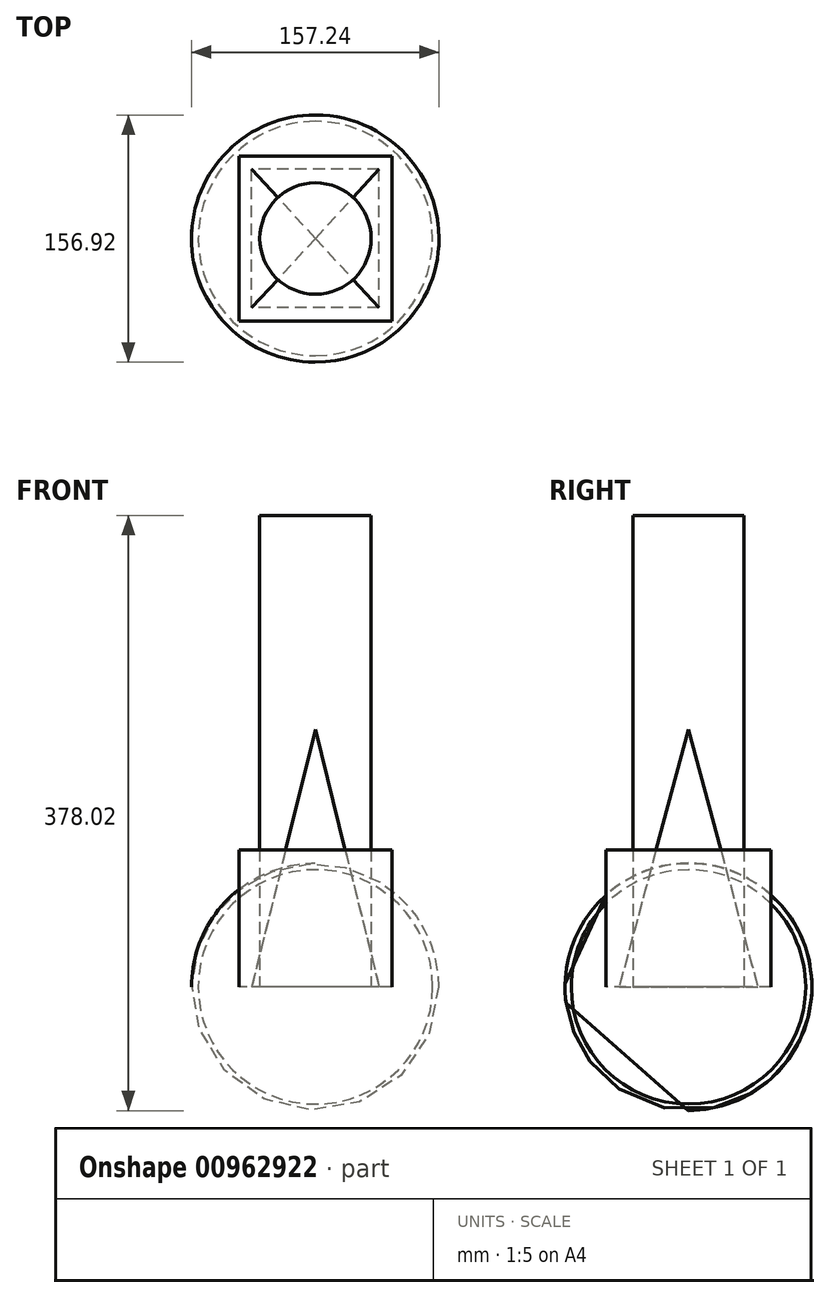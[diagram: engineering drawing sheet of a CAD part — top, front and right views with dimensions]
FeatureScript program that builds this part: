
annotation { "Feature Type Name" : "Feature", "Feature Type Description" : "" }
export const myFeature = defineFeature(function(context is Context, id is Id, definition is map)
    precondition{}
    {
        {
            var Q0;
            Q0=qCreatedBy(makeId("Top.planeOp"),FACE);
            var sketch = newSketch(context, id + "F0", { "sketchPlane" : qUnion([Q0])});
            skArc(sketch, "E0", {"start": v(0, 78.46) * mm, "mid": v(-78.46, 0.16) * mm, "end": v(-0.32, -78.46) * mm});
            skLineSegment(sketch, "E1", {"start": v(0, 78.46) * mm, "end": v(-0.32, -78.46) * mm});
            skSolve(sketch);
        }
        {
            var Q0;
            Q0=makeQuery(id+"F0.imprint","IMPRINT",FACE,{"disambiguationData":[TD([[makeQuery(id+"F0.imprint","IMPRINT",EDGE,{"derivedFrom":sQuery(id+"F0.wireOp",EDGE,"E0")}),1.0]])]});
            var Q1;
            Q1=sQuery(id+"F0.wireOp",EDGE,"E1");
            revolve(context, id + "F1", {"surfaceOperationType" : NewSurfaceOperationType.NEW, "entities" : qUnion([Q0]), "axis" : qUnion([Q1]), "revolveType" : RevolveType.FULL});
        }
        {
            var Q0;
            Q0=qCreatedBy(makeId("Top.planeOp"),FACE);
            var sketch = newSketch(context, id + "F2", { "sketchPlane" : qUnion([Q0])});
            skLineSegment(sketch, "E2.bottom", {"start": v(40.46, -44) * mm, "end": v(-40.46, -44) * mm});
            skLineSegment(sketch, "E2.top", {"start": v(40.46, 44) * mm, "end": v(-40.46, 44) * mm});
            skLineSegment(sketch, "E2.left", {"start": v(40.46, -44) * mm, "end": v(40.46, 44) * mm});
            skLineSegment(sketch, "E2.right", {"start": v(-40.46, -44) * mm, "end": v(-40.46, 44) * mm});
            skPoint(sketch, "E2.middle", {"position": v(0, 0) * mm});
            skSolve(sketch);
        }
        {
            var Q0;
            Q0=qCreatedBy(makeId("Front.planeOp"),FACE);
            var sketch = newSketch(context, id + "F3", { "sketchPlane" : qUnion([Q0])});
            skPoint(sketch, "E3", {"position": v(0, 163.51) * mm});
            skSolve(sketch);
        }
        {
            var Q0;
            Q0=sQuery(id+"F3.wireOp",VERTEX,"E3");
            var Q1;
            Q1 = qSketchRegion(id + "F2", true);
            loft(context, id + "F4", {"sheetProfilesArray" : [{ "sheetProfileEntities" : qUnion([Q0]) }, { "sheetProfileEntities" : qUnion([Q1]) }]});
        }
        {
            var Q0;
            Q0=qCreatedBy(makeId("Top.planeOp"),FACE);
            var sketch = newSketch(context, id + "F5", { "sketchPlane" : qUnion([Q0])});
            skCircle(sketch, "E4", {"center": v(0, 0) * mm, "radius": 35.35 * mm});
            skSolve(sketch);
        }
        {
            var Q0;
            Q0=makeQuery(id+"F5.imprint","IMPRINT",FACE,{"disambiguationData":[TD([[makeQuery(id+"F5.imprint","IMPRINT",EDGE,{"derivedFrom":sQuery(id+"F5.wireOp",EDGE,"E4")}),1.0]])]});
            extrude(context, id + "F6", {"entities" : qUnion([Q0]), "depth" : 299.4 * mm, "offsetDistance" : 25.4 * mm});
        }
        {
            var Q0;
            Q0=qCreatedBy(makeId("Top.planeOp"),FACE);
            var sketch = newSketch(context, id + "F7", { "sketchPlane" : qUnion([Q0])});
            skArc(sketch, "E5", {"start": v(0, 74.44) * mm, "mid": v(-74.44, 0) * mm, "end": v(0, -74.44) * mm});
            skLineSegment(sketch, "E6", {"start": v(0, 74.44) * mm, "end": v(0, -74.44) * mm});
            skSolve(sketch);
        }
        {
            var Q0;
            Q0=makeQuery(id+"F7.imprint","IMPRINT",FACE,{"disambiguationData":[TD([[makeQuery(id+"F7.imprint","IMPRINT",EDGE,{"derivedFrom":sQuery(id+"F7.wireOp",EDGE,"E5")}),1.0]])]});
            var Q1;
            Q1=sQuery(id+"F7.wireOp",EDGE,"E6");
            revolve(context, id + "F8", {"surfaceOperationType" : NewSurfaceOperationType.NEW, "entities" : qUnion([Q0]), "axis" : qUnion([Q1]), "revolveType" : RevolveType.FULL});
        }
        {
            var Q0;
            Q0=qCreatedBy(makeId("Top.planeOp"),FACE);
            var sketch = newSketch(context, id + "F9", { "sketchPlane" : qUnion([Q0])});
            skLineSegment(sketch, "E7.bottom", {"start": v(48.5, 52.43) * mm, "end": v(-48.5, 52.43) * mm});
            skLineSegment(sketch, "E7.top", {"start": v(48.5, -52.43) * mm, "end": v(-48.5, -52.43) * mm});
            skLineSegment(sketch, "E7.left", {"start": v(48.5, 52.43) * mm, "end": v(48.5, -52.43) * mm});
            skLineSegment(sketch, "E7.right", {"start": v(-48.5, 52.43) * mm, "end": v(-48.5, -52.43) * mm});
            skPoint(sketch, "E7.middle", {"position": v(0, 0) * mm});
            skSolve(sketch);
        }
        {
            var Q0;
            Q0=makeQuery(id+"F9.imprint","IMPRINT",FACE,{"disambiguationData":[TD([[makeQuery(id+"F9.imprint","IMPRINT",EDGE,{"derivedFrom":sQuery(id+"F9.wireOp",EDGE,"E7.bottom")}),1.0]])]});
            extrude(context, id + "F10", {"entities" : qUnion([Q0]), "depth" : 87.15 * mm, "offsetDistance" : 25.4 * mm});
        }
        {
            var Q0;
            Q0=qCreatedBy(makeId("Right.planeOp"),FACE);
            var sketch = newSketch(context, id + "F11", { "sketchPlane" : qUnion([Q0])});
            skCircle(sketch, "E8", {"center": v(0, 0) * mm, "radius": 54.68 * mm});
            skSolve(sketch);
        }
        {
            var Q0;
            Q0=qCreatedBy(makeId("Front.planeOp"),FACE);
            var sketch = newSketch(context, id + "F12", { "sketchPlane" : qUnion([Q0])});
            skPoint(sketch, "E9", {"position": v(-202.86, 0) * mm});
            skSolve(sketch);
        }
        {
            var Q0;
            Q0=sQuery(id+"F11.wireOp",EDGE,"E8");
            var Q1;
            Q1=sQuery(id+"F12.wireOp",VERTEX,"E9");
            loft(context, id + "F13", {"bodyType" : ToolBodyType.SURFACE, "wireProfilesArray" : [{ "wireProfileEntities" : qUnion([Q0]) }, { "wireProfileEntities" : qUnion([Q1]) }]});
        }
    });
